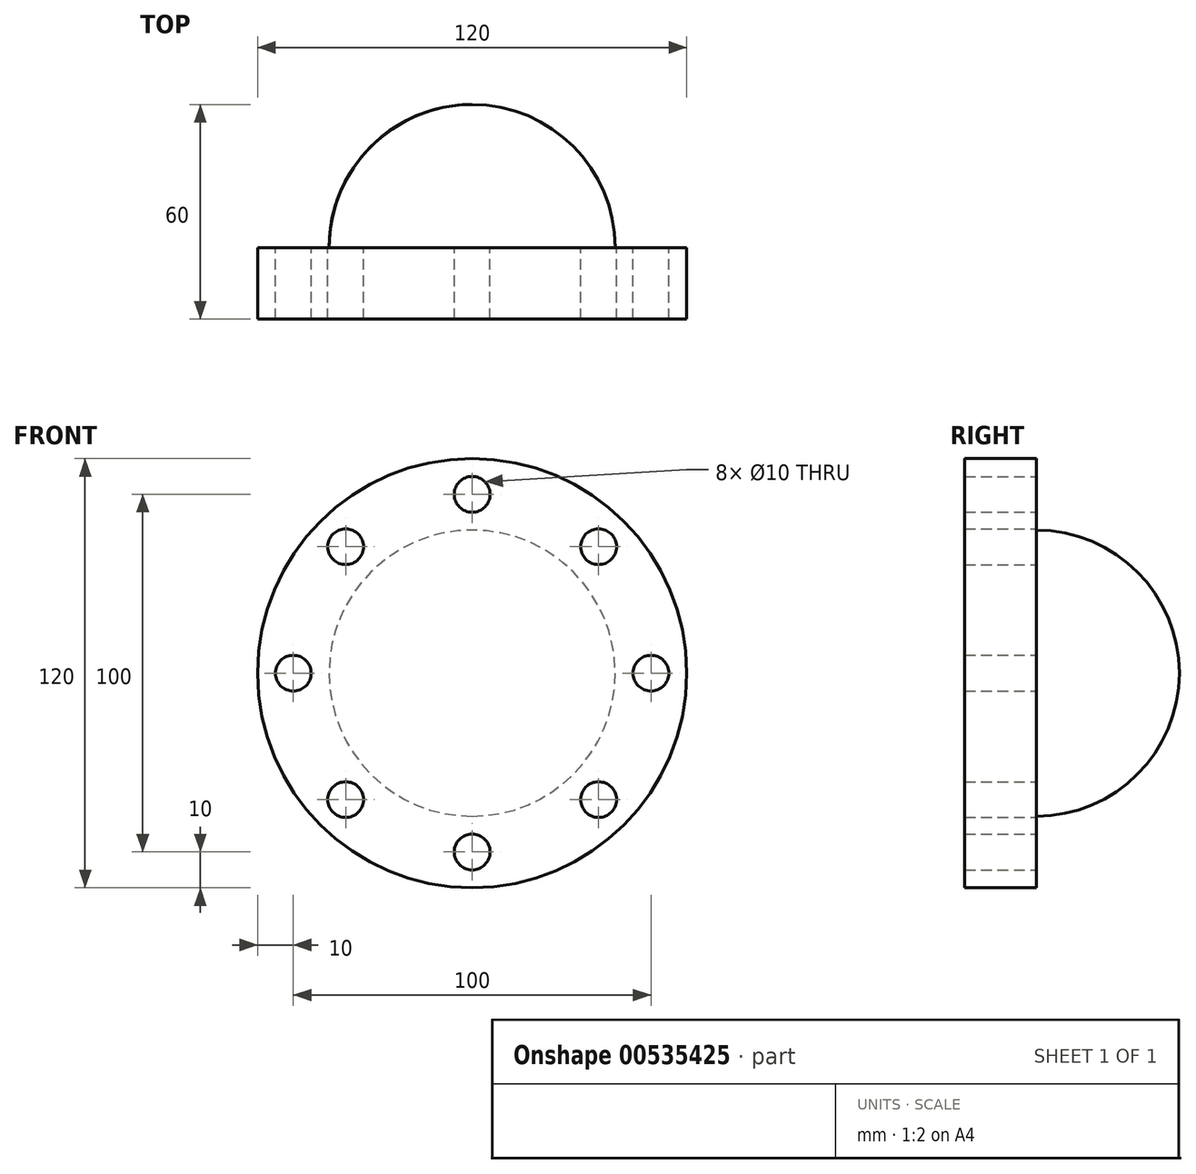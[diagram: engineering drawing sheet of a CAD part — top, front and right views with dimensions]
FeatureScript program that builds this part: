
annotation { "Feature Type Name" : "Feature", "Feature Type Description" : "" }
export const myFeature = defineFeature(function(context is Context, id is Id, definition is map)
    precondition{}
    {
        {
            var Q0;
            Q0=qCreatedBy(makeId("Front.planeOp"),FACE);
            var sketch = newSketch(context, id + "F0", { "sketchPlane" : qUnion([Q0])});
            skCircle(sketch, "E0", {"center": v(0, 0) * mm, "radius": 60 * mm});
            skCircle(sketch, "E1", {"center": v(0, 50) * mm, "radius": 5 * mm});
            skCircle(sketch, "E2.1.0", {"center": v(-35.36, 35.36) * mm, "radius": 5 * mm});
            skCircle(sketch, "E2.2.0", {"center": v(-50, 0) * mm, "radius": 5 * mm});
            skCircle(sketch, "E2.3.0", {"center": v(-35.36, -35.36) * mm, "radius": 5 * mm});
            skCircle(sketch, "E2.4.0", {"center": v(0, -50) * mm, "radius": 5 * mm});
            skCircle(sketch, "E2.5.0", {"center": v(35.36, -35.36) * mm, "radius": 5 * mm});
            skCircle(sketch, "E2.6.0", {"center": v(50, 0) * mm, "radius": 5 * mm});
            skCircle(sketch, "E2.7.0", {"center": v(35.36, 35.36) * mm, "radius": 5 * mm});
            skSolve(sketch);
        }
        {
            var Q0;
            Q0=makeQuery(id+"F0.imprint","IMPRINT",FACE,{"disambiguationData":[TD([[makeQuery(id+"F0.imprint","IMPRINT",EDGE,{"derivedFrom":sQuery(id+"F0.wireOp",EDGE,"E0")}),1.0]])]});
            extrude(context, id + "F1", {"entities" : qUnion([Q0]), "depth" : 20 * mm, "offsetDistance" : 25 * mm});
        }
        {
            var Q0;
            Q0=qCreatedBy(makeId("Top.planeOp"),FACE);
            var sketch = newSketch(context, id + "F2", { "sketchPlane" : qUnion([Q0])});
            skLineSegment(sketch, "E3", {"start": v(60, 0) * mm, "end": v(60, -20) * mm});
            skLineSegment(sketch, "E4", {"start": v(-60, -20) * mm, "end": v(-60, 0) * mm});
            skArc(sketch, "E5", {"start": v(0, 40) * mm, "mid": v(-28.28, 28.28) * mm, "end": v(-40, 0) * mm});
            skLineSegment(sketch, "E6", {"start": v(0, 0) * mm, "end": v(0, 40) * mm});
            skLineSegment(sketch, "E7.0", {"start": v(0, 0) * mm, "end": v(-40, 0) * mm});
            skPoint(sketch, "E8.orphan", {"position": v(60, 0) * mm});
            skPoint(sketch, "E9.orphan", {"position": v(-60, 0) * mm});
            skSolve(sketch);
        }
        {
            var Q0;
            Q0 = qSketchRegion(id + "F2", true);
            var Q1;
            Q1=sQuery(id+"F2.wireOp",EDGE,"E6");
            revolve(context, id + "F3", {"operationType" : NewBodyOperationType.ADD, "entities" : qUnion([Q0]), "axis" : qUnion([Q1]), "revolveType" : RevolveType.FULL});
        }
    });
